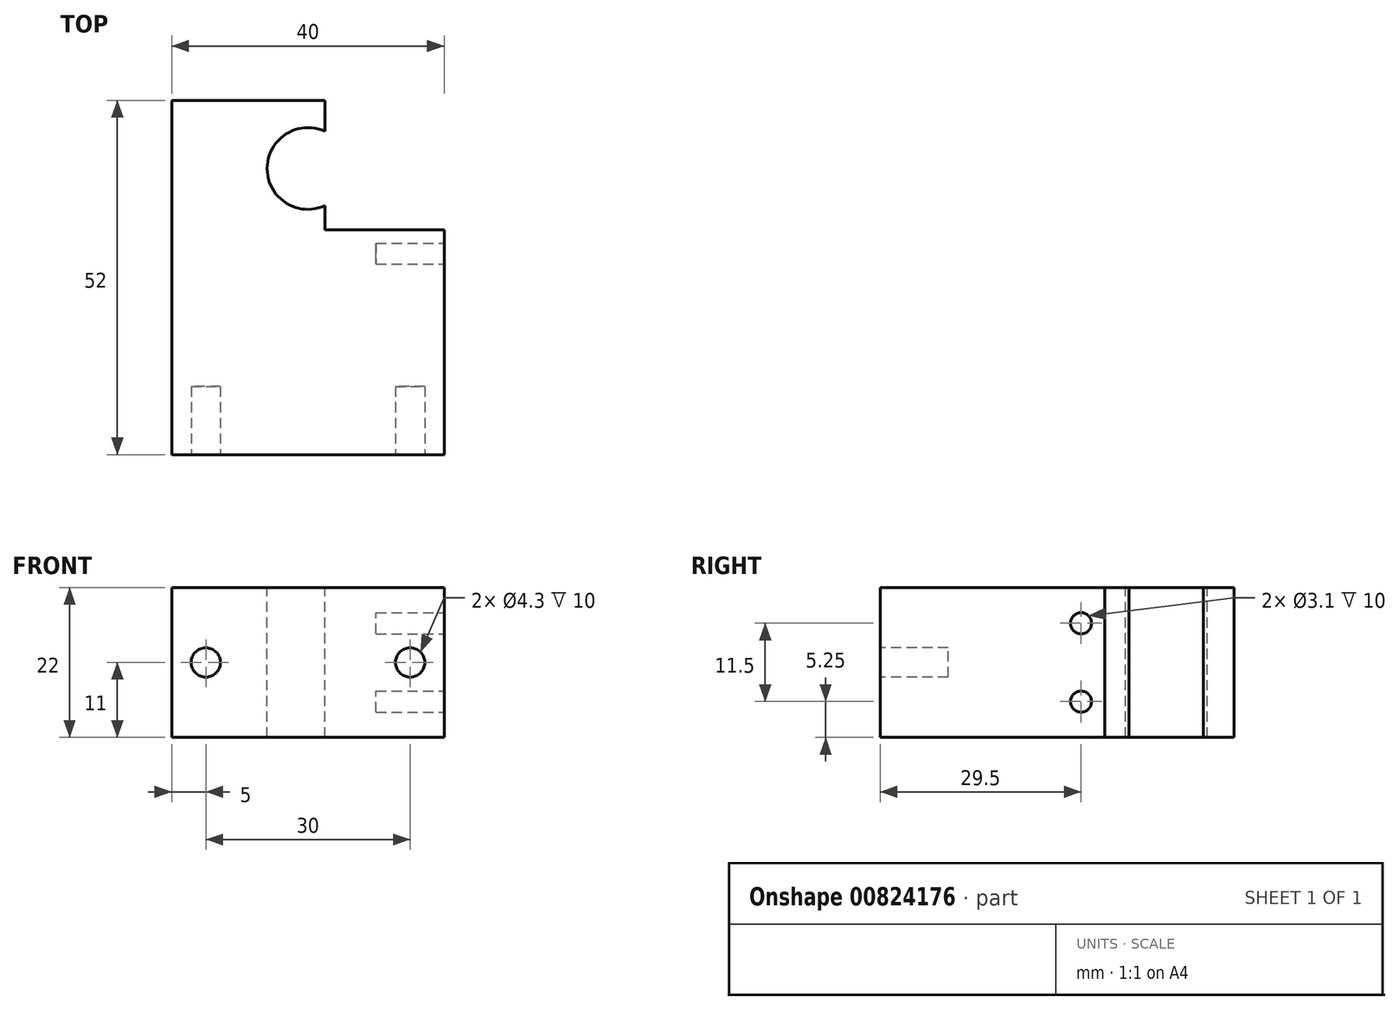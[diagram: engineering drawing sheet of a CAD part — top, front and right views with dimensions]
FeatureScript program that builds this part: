
annotation { "Feature Type Name" : "Feature", "Feature Type Description" : "" }
export const myFeature = defineFeature(function(context is Context, id is Id, definition is map)
    precondition{}
    {
        {
            var Q0;
            Q0=qCreatedBy(makeId("Top.planeOp"),FACE);
            var sketch = newSketch(context, id + "F0", { "sketchPlane" : qUnion([Q0])});
            skLineSegment(sketch, "E0.bottom", {"start": v(0, 0) * mm, "end": v(40, 0) * mm});
            skLineSegment(sketch, "E0.top", {"start": v(0, 52) * mm, "end": v(40, 52) * mm});
            skLineSegment(sketch, "E0.left", {"start": v(0, 0) * mm, "end": v(0, 52) * mm});
            skLineSegment(sketch, "E0.right", {"start": v(40, 0) * mm, "end": v(40, 52) * mm});
            skSolve(sketch);
        }
        {
            var Q0;
            Q0 = qSketchRegion(id + "F0", true);
            extrude(context, id + "F1", {"entities" : qUnion([Q0]), "depth" : 22 * mm, "offsetDistance" : 25 * mm});
        }
        {
            var Q0;
            Q0=makeQuery(id+"F1.opExtrude","CAP_FACE",FACE,{"disambiguationData":[OSD([sQuery(id+"F0.wireOp",EDGE,"E0.bottom"),sQuery(id+"F0.wireOp",EDGE,"E0.top"),sQuery(id+"F0.wireOp",EDGE,"E0.left"),sQuery(id+"F0.wireOp",EDGE,"E0.right")])],"isStart":false});
            var sketch = newSketch(context, id + "F2", { "sketchPlane" : qUnion([Q0])});
            skSolve(sketch);
        }
        {
            var Q0;
            Q0=makeQuery(id+"F2.imprint","IMPRINT",FACE,{"disambiguationData":[TD([[makeQuery(id+"F2.imprint","IMPRINT",EDGE,{"derivedFrom":makeQuery(id+"F1.opExtrude","CAP_EDGE",EDGE,{"disambiguationData":[OSD([sQuery(id+"F0.wireOp",EDGE,"E0.bottom")])],"isStart":false})}),1.0]])]});
            var sketch = newSketch(context, id + "F3", { "sketchPlane" : qUnion([Q0])});
            skLineSegment(sketch, "E1", {"start": v(0, 0) * mm, "end": v(0, 52) * mm, "construction": true});
            skLineSegment(sketch, "E2", {"start": v(0, 0) * mm, "end": v(40, 0) * mm, "construction": true});
            skLineSegment(sketch, "E3", {"start": v(20, 0) * mm, "end": v(20, 52) * mm, "construction": true});
            skLineSegment(sketch, "E4", {"start": v(0, 52) * mm, "end": v(20, 52) * mm, "construction": true});
            skPoint(sketch, "E5.orphan", {"position": v(20, 53.79) * mm});
            skCircle(sketch, "E6", {"center": v(20, 42) * mm, "radius": 6 * mm});
            skSolve(sketch);
        }
        {
            var Q0;
            Q0 = qSketchRegion(id + "F3", true);
            extrude(context, id + "F4", {"entities" : qUnion([Q0]), "operationType" : NewBodyOperationType.REMOVE, "oppositeDirection" : true, "depth" : 25 * mm, "offsetDistance" : 25 * mm});
        }
        {
            var Q0;
            Q0=makeQuery(id+"F1.opExtrude","SWEPT_FACE",FACE,{"disambiguationData":[OSD([sQuery(id+"F0.wireOp",EDGE,"E0.bottom")])]});
            var sketch = newSketch(context, id + "F5", { "sketchPlane" : qUnion([Q0])});
            skLineSegment(sketch, "E7", {"start": v(0, 11) * mm, "end": v(40, 11) * mm, "construction": true});
            skCircle(sketch, "E8", {"center": v(5, 11) * mm, "radius": 2.15 * mm});
            skCircle(sketch, "E9", {"center": v(35, 11) * mm, "radius": 2.15 * mm});
            skLineSegment(sketch, "E10", {"start": v(20, 22) * mm, "end": v(20, 0) * mm, "construction": true});
            skSolve(sketch);
        }
        {
            var Q0;
            Q0 = qSketchRegion(id + "F5", true);
            extrude(context, id + "F6", {"entities" : qUnion([Q0]), "operationType" : NewBodyOperationType.REMOVE, "oppositeDirection" : true, "depth" : 10 * mm, "offsetDistance" : 25 * mm});
        }
        {
            var Q0;
            Q0=makeQuery(id+"F1.opExtrude","SWEPT_FACE",FACE,{"disambiguationData":[OSD([sQuery(id+"F0.wireOp",EDGE,"E0.top")])]});
            var sketch = newSketch(context, id + "F7", { "sketchPlane" : qUnion([Q0])});
            skLineSegment(sketch, "E11.bottom", {"start": v(-40, 0) * mm, "end": v(-22.5, 0) * mm});
            skLineSegment(sketch, "E11.top", {"start": v(-40, 22) * mm, "end": v(-22.5, 22) * mm});
            skLineSegment(sketch, "E11.left", {"start": v(-40, 0) * mm, "end": v(-40, 22) * mm});
            skLineSegment(sketch, "E11.right", {"start": v(-22.5, 0) * mm, "end": v(-22.5, 22) * mm});
            skSolve(sketch);
        }
        {
            var Q0;
            Q0 = qSketchRegion(id + "F7", true);
            extrude(context, id + "F8", {"entities" : qUnion([Q0]), "operationType" : NewBodyOperationType.REMOVE, "oppositeDirection" : true, "depth" : 19 * mm, "offsetDistance" : 25 * mm});
        }
        {
            var Q0;
            Q0=makeQuery(id+"F1.opExtrude","SWEPT_FACE",FACE,{"disambiguationData":[OSD([sQuery(id+"F0.wireOp",EDGE,"E0.right")])]});
            var sketch = newSketch(context, id + "F9", { "sketchPlane" : qUnion([Q0])});
            skLineSegment(sketch, "E12", {"start": v(29.5, 22) * mm, "end": v(29.5, 0) * mm, "construction": true});
            skCircle(sketch, "E13", {"center": v(29.5, 16.75) * mm, "radius": 1.55 * mm});
            skCircle(sketch, "E14", {"center": v(29.5, 5.25) * mm, "radius": 1.55 * mm});
            skLineSegment(sketch, "E15", {"start": v(33, 11) * mm, "end": v(14.1, 11) * mm, "construction": true});
            skLineSegment(sketch, "E16", {"start": v(33, 11) * mm, "end": v(72.93, 11) * mm, "construction": true});
            skSolve(sketch);
        }
        {
            var Q0;
            Q0 = qSketchRegion(id + "F9", true);
            extrude(context, id + "F10", {"entities" : qUnion([Q0]), "operationType" : NewBodyOperationType.REMOVE, "oppositeDirection" : true, "depth" : 10 * mm, "offsetDistance" : 25 * mm});
        }
    });
